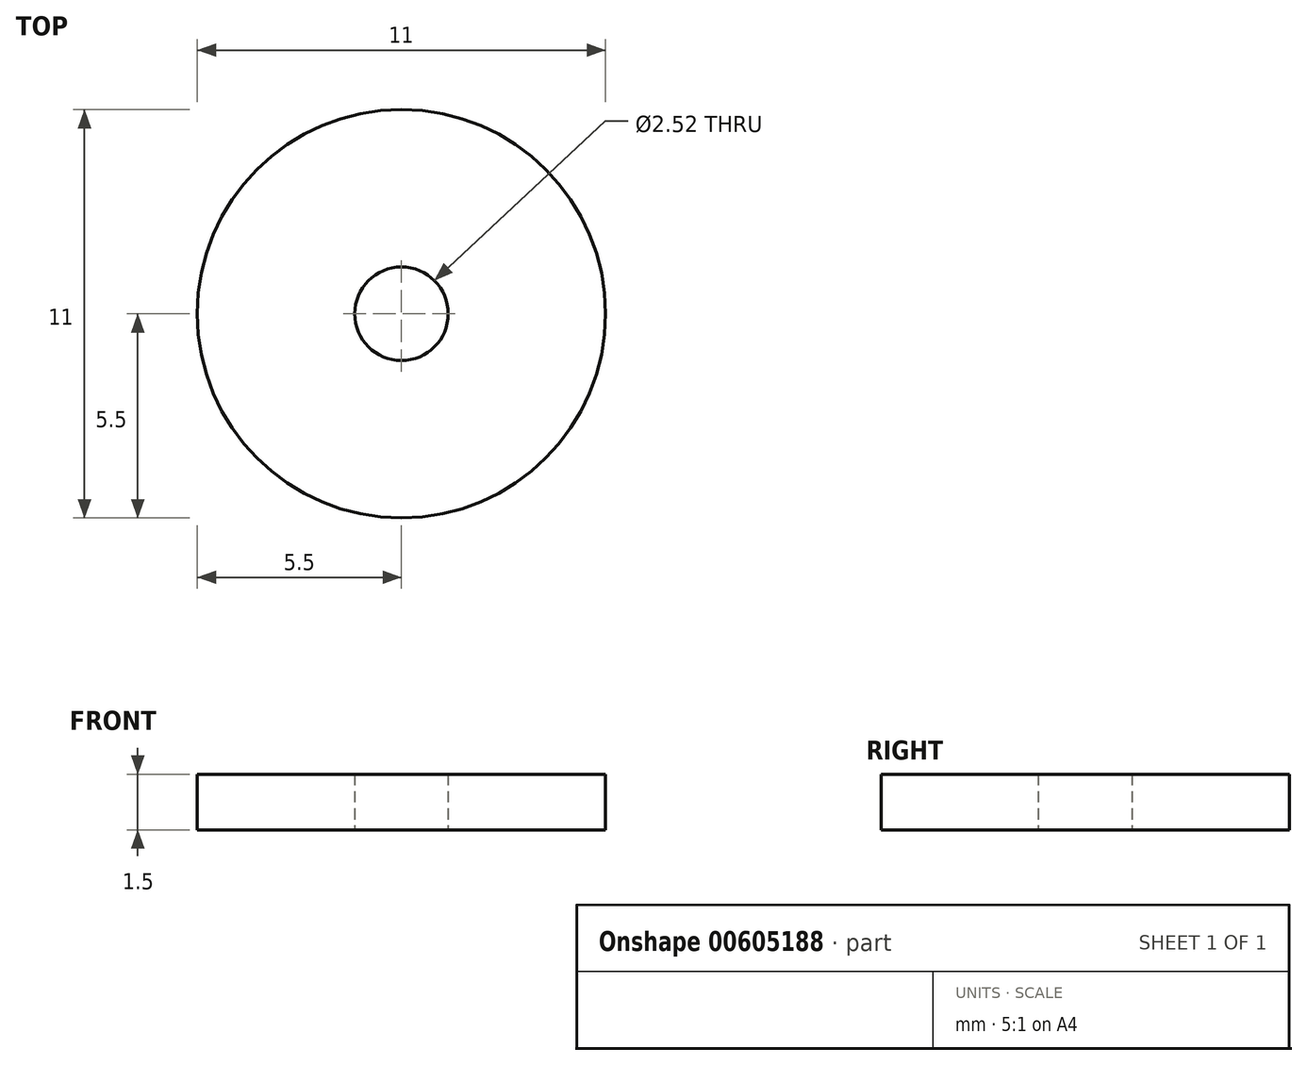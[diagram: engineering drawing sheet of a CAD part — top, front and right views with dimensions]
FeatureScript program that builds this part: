
annotation { "Feature Type Name" : "Feature", "Feature Type Description" : "" }
export const myFeature = defineFeature(function(context is Context, id is Id, definition is map)
    precondition{}
    {
        {
            var Q0;
            Q0=qCreatedBy(makeId("Top.planeOp"),FACE);
            var sketch = newSketch(context, id + "F0", { "sketchPlane" : qUnion([Q0])});
            skCircle(sketch, "E0", {"center": v(0, 0) * mm, "radius": 5.5 * mm});
            skCircle(sketch, "E1", {"center": v(0, 0) * mm, "radius": 1.26 * mm});
            skSolve(sketch);
        }
        {
            var Q0;
            Q0=makeQuery(id+"F0.imprint","IMPRINT",FACE,{"disambiguationData":[TD([[makeQuery(id+"F0.imprint","IMPRINT",EDGE,{"derivedFrom":sQuery(id+"F0.wireOp",EDGE,"E0")}),1.0]])]});
            extrude(context, id + "F1", {"entities" : qUnion([Q0]), "depth" : 1.5 * mm, "offsetDistance" : 25 * mm});
        }
    });
